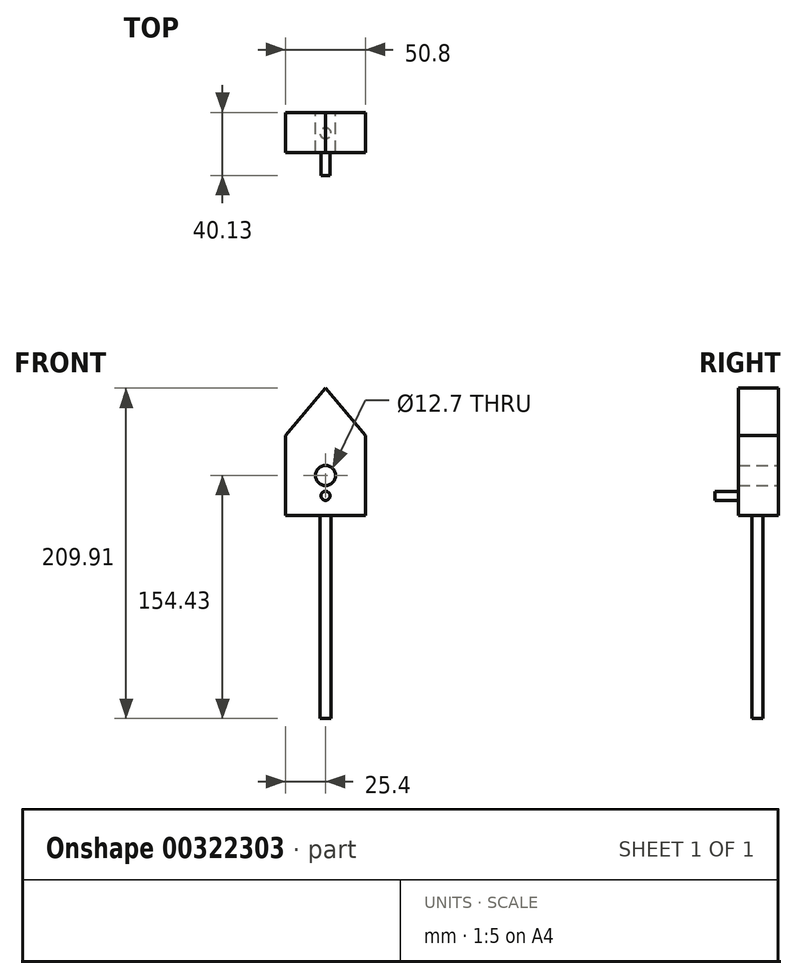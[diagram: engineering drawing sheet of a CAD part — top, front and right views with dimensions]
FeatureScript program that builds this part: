
annotation { "Feature Type Name" : "Feature", "Feature Type Description" : "" }
export const myFeature = defineFeature(function(context is Context, id is Id, definition is map)
    precondition{}
    {
        {
            var Q0;
            Q0=qCreatedBy(makeId("Front.planeOp"),FACE);
            var sketch = newSketch(context, id + "F0", { "sketchPlane" : qUnion([Q0])});
            skLineSegment(sketch, "E0.top", {"start": v(25.4, -25.4) * mm, "end": v(-25.4, -25.4) * mm});
            skLineSegment(sketch, "E0.left", {"start": v(25.4, 25.4) * mm, "end": v(25.4, -25.4) * mm});
            skLineSegment(sketch, "E0.right", {"start": v(-25.4, 25.4) * mm, "end": v(-25.4, -25.4) * mm});
            skPoint(sketch, "E0.middle", {"position": v(0, 0) * mm});
            skLineSegment(sketch, "E1", {"start": v(-25.4, 25.4) * mm, "end": v(0, 55.48) * mm});
            skLineSegment(sketch, "E2", {"start": v(0, 55.48) * mm, "end": v(25.4, 25.4) * mm});
            skCircle(sketch, "E3", {"center": v(0, 0) * mm, "radius": 6.35 * mm});
            skSolve(sketch);
        }
        {
            var Q0;
            Q0 = qSketchRegion(id + "F0", true);
            extrude(context, id + "F1", {"entities" : qUnion([Q0]), "depth" : 25.4 * mm});
        }
        {
            var Q0;
            Q0=makeQuery(id+"F1.opExtrude","CAP_FACE",FACE,{"disambiguationData":[OSD([sQuery(id+"F0.wireOp",EDGE,"E0.top"),sQuery(id+"F0.wireOp",EDGE,"E0.left"),sQuery(id+"F0.wireOp",EDGE,"E0.right"),sQuery(id+"F0.wireOp",EDGE,"E1"),sQuery(id+"F0.wireOp",EDGE,"E2"),sQuery(id+"F0.wireOp",EDGE,"E3")])],"isStart":false});
            var sketch = newSketch(context, id + "F2", { "sketchPlane" : qUnion([Q0])});
            skCircle(sketch, "E4", {"center": v(0, -12.95) * mm, "radius": 2.88 * mm});
            skSolve(sketch);
        }
        {
            var Q0;
            Q0 = qSketchRegion(id + "F2", true);
            extrude(context, id + "F3", {"entities" : qUnion([Q0]), "operationType" : NewBodyOperationType.ADD, "depth" : 14.73 * mm});
        }
        {
            var Q0;
            Q0=makeQuery(id+"F1.opExtrude","SWEPT_FACE",FACE,{"disambiguationData":[OSD([sQuery(id+"F0.wireOp",EDGE,"E0.top")])]});
            var sketch = newSketch(context, id + "F4", { "sketchPlane" : qUnion([Q0])});
            skCircle(sketch, "E5", {"center": v(0, 13.26) * mm, "radius": 3.48 * mm});
            skSolve(sketch);
        }
        {
            var Q0;
            Q0 = qSketchRegion(id + "F4", true);
            extrude(context, id + "F5", {"entities" : qUnion([Q0]), "operationType" : NewBodyOperationType.ADD, "depth" : 129.03 * mm});
        }
    });
